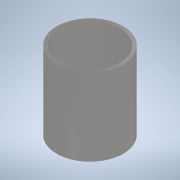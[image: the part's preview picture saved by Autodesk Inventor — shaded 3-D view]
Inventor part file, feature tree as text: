
AUTODESK INVENTOR PART (.ipt)
format: ipt  version: 2022 (Build 260153000, 153)  size: 100,352 bytes
history: native  units: in
note: dims shown in document units (in); Inventor stores cm internally (conversion verified against a paired STEP export)
features: extrude x1, sketch x1
ambient origin geometry x8: Origin, YZ Plane, XZ Plane, XY Plane, X Axis, Y Axis, Z Axis, Center Point
bodies: Solid1 (feature_tree)
feature tree (2):
  extrude  "Extrusion1"  Depth=0.689in
  sketch  "Sketch1"  dims[d0=0.5906in d1=0.0295in d2=0.689in d3=0.0in]
